# Revit family: Door-Counter_FaceOfWallMount_CornellIron
name_source: partatom
category: Doors
revit_build: Autodesk Revit MEP 2013 (Build: 20130531_2115(x64)
units: mm (PartAtom-declared; Revit-internal decimal feet)

## types (9) — shared parameters
04 CSI = 08 33 00
95 CSI = 08330
Assembly Code = B2030410
Coil Dimension Note = 8” to 14” - Consult Cornell when dimensions are critical.
Crank Height = 5' - 4"
Description = Built to order metal slatted rolling doors secure openings above counters. Can fully close to the floor.
Distributor Locator = http://www.cornelliron.com
From Coil Side Operate on Left = No
From Coil Side Operate on Right = Yes
Function = Interior
Height = 8' - 0"
Jamb Dimension Note = 2 1/2” wide. Consult Cornell when dimensions are critical.
LEED Information = http://www.cornelliron.com
Manufacturer = Cornell Iron Works
Model = ESC10
Mounting = Face of Wall
Optional Powder Coat Finish = No
Optional aluminum, color anodized finish = No
Product Options = Countertops by Cornell, Integral Frame and Countertop Units, Perforated curtain slats, graphic images on door curtain
Representative Disclaimer = Cornell products are sold and installed through a nationwide network of independent distributors.
Revit Object Download Link = http://cornellcookson.smartbim.com
Sizing Disclaimer = 21' Wide or 10' High Standard Construction
Subcategory = Overhead Doors
URL = http://www.cornelliron.com
URL CAD = http://www.cornelliron.com
URL Photographs = http://www.cornelliron.com
URL Specifications = http://www.cornelliron.com
Wall Closure = By host
Wall Construction = Drywall, wood, masonry, steel
Width = 6' - 0"

## per-type parameters (varying)
| type | Bottom Bar | Curtain 1 1/2" slat | Drip Extension | Guide Height | Guides | Hand Crank | Hood | Motor | Operator |
| Motor Operated, Aluminium (Anodized Finish) | Aluminum, anodized finish (non-curtain components) | Aluminum, anodized finish (curtain only) | 0' - 5" | 8' - 5" | Aluminum, anodized finish (non-curtain components) | No | Aluminum, anodized finish (non-curtain components) | Yes | Operator : Motor Operated |
| Hand-Crank Operated, Aluminium (Anodized Finish) | Aluminum, anodized finish (non-curtain components) | Aluminum, anodized finish (curtain only) | 0' - 3" | 8' - 3" | Aluminum, anodized finish (non-curtain components) | Yes | Aluminum, anodized finish (non-curtain components) | No | Operator : Hand-Crank |
| Hand-Crank Operated, Galvanized Steel | Galvanized or powder coated plain steel (non curtain components) | Galvanized steel (curtain only) | 0' - 3" | 8' - 3" | Galvanized or powder coated plain steel (non curtain components) | Yes | Galvanized or powder coated plain steel (non curtain components) | No | Operator : Hand-Crank |
| Hand-Crank Operated, Stainless Steel | Stainless steel (non-curtain components) | Stainless steel (curtain only) | 0' - 3" | 8' - 3" | Stainless steel (non-curtain components) | Yes | Stainless steel (non-curtain components) | No | Operator : Hand-Crank |
| Motor Operated, Galvanized Steel | Galvanized or powder coated plain steel (non curtain components) | Galvanized steel (curtain only) | 0' - 5" | 8' - 5" | Galvanized or powder coated plain steel (non curtain components) | No | Galvanized or powder coated plain steel (non curtain components) | Yes | Operator : Motor Operated |
| Motor Operated, Stainless Steel | Stainless steel (non-curtain components) | Stainless steel (curtain only) | 0' - 5" | 8' - 5" | Stainless steel (non-curtain components) | No | Stainless steel (non-curtain components) | Yes | Operator : Motor Operated |
| Push-Up Operated, Aluminium (Anodized Finish) | Aluminum, anodized finish (non-curtain components) | Aluminum, anodized finish (curtain only) | 0' - 3" | 8' - 3" | Aluminum, anodized finish (non-curtain components) | No | Aluminum, anodized finish (non-curtain components) | No | Operator : Push-UP |
| Push-Up Operated, Galvanized Steel | Galvanized or powder coated plain steel (non curtain components) | Galvanized steel (curtain only) | 0' - 3" | 8' - 3" | Galvanized or powder coated plain steel (non curtain components) | No | Galvanized or powder coated plain steel (non curtain components) | No | Operator : Push-UP |
| Push-Up Operated, Stainless Steel | Stainless steel (non-curtain components) | Stainless steel (curtain only) | 0' - 3" | 8' - 3" | Stainless steel (non-curtain components) | No | Stainless steel (non-curtain components) | No | Operator : Push-UP |

## geometry (parser evidence)
native form markers: Blend x24, Sweep x15
no freeform markers — native parametric forms only
